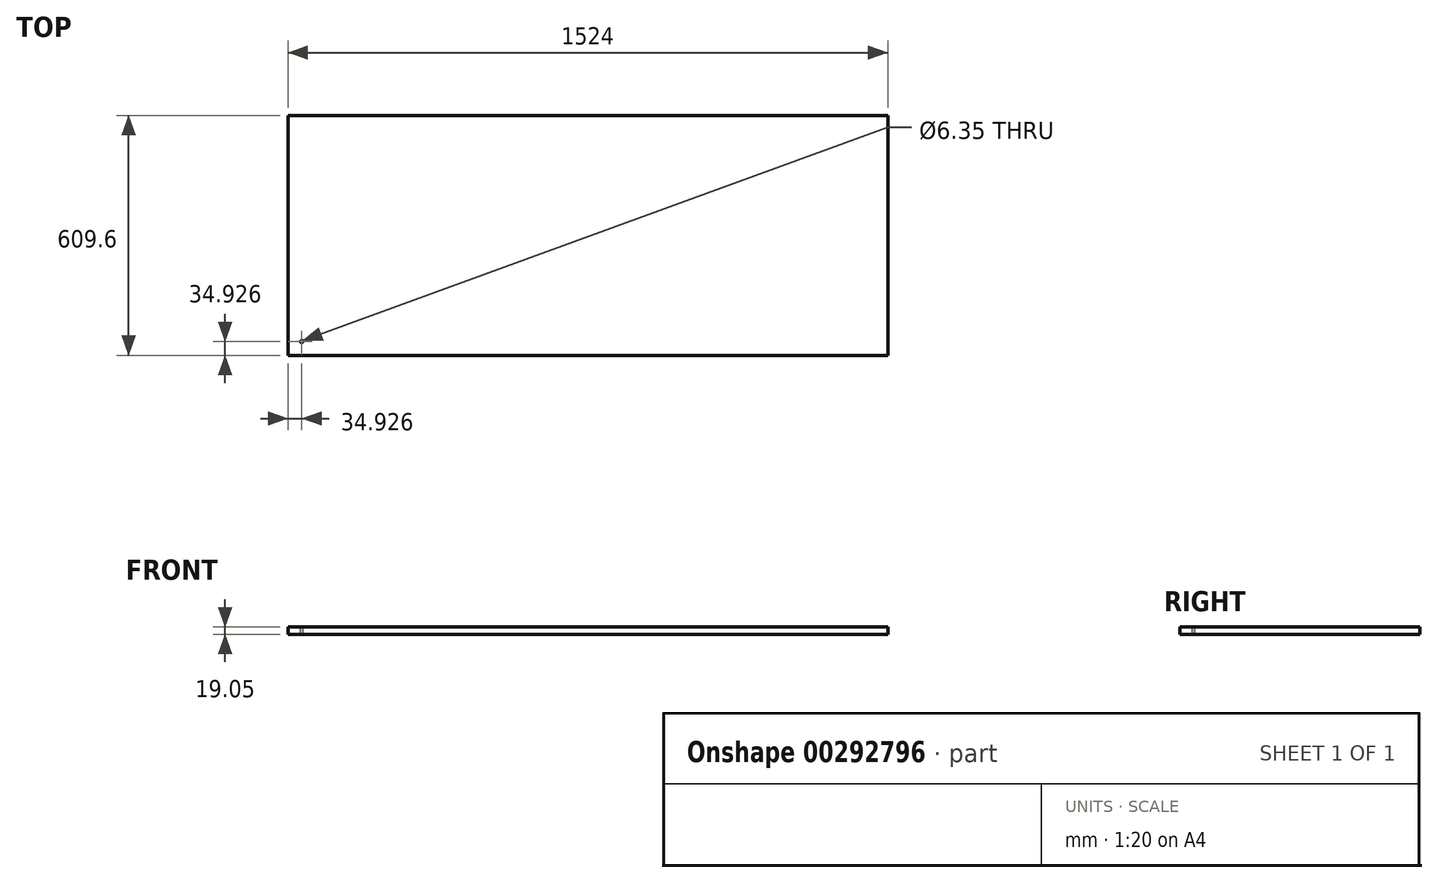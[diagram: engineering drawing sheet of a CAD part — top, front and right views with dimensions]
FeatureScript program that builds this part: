
annotation { "Feature Type Name" : "Feature", "Feature Type Description" : "" }
export const myFeature = defineFeature(function(context is Context, id is Id, definition is map)
    precondition{}
    {
        {
            var Q0;
            Q0=qCreatedBy(makeId("Top.planeOp"),FACE);
            var sketch = newSketch(context, id + "F0", { "sketchPlane" : qUnion([Q0])});
            skLineSegment(sketch, "E0.bottom", {"start": v(-1132.59, -308.04) * mm, "end": v(391.41, -308.04) * mm});
            skLineSegment(sketch, "E0.top", {"start": v(-1132.59, 301.56) * mm, "end": v(391.41, 301.56) * mm});
            skLineSegment(sketch, "E0.left", {"start": v(-1132.59, -308.04) * mm, "end": v(-1132.59, 301.56) * mm});
            skLineSegment(sketch, "E0.right", {"start": v(391.41, -308.04) * mm, "end": v(391.41, 301.56) * mm});
            skSolve(sketch);
        }
        {
            var Q0;
            Q0 = qSketchRegion(id + "F0", true);
            extrude(context, id + "F1", {"entities" : qUnion([Q0]), "depth" : 19.05 * mm});
        }
        {
            var Q0;
            Q0=makeQuery(id+"F1.opExtrude","CAP_FACE",FACE,{"disambiguationData":[OSD([sQuery(id+"F0.wireOp",EDGE,"E0.bottom"),sQuery(id+"F0.wireOp",EDGE,"E0.top"),sQuery(id+"F0.wireOp",EDGE,"E0.left"),sQuery(id+"F0.wireOp",EDGE,"E0.right")])],"isStart":false});
            var sketch = newSketch(context, id + "F2", { "sketchPlane" : qUnion([Q0])});
            skCircle(sketch, "E1", {"center": v(-1097.66, -273.11) * mm, "radius": 3.18 * mm});
            skSolve(sketch);
        }
        {
            var Q0;
            Q0=sQuery(id+"F2.wireOp",VERTEX,"E1.center");
            var Q1;
            Q1=makeQuery(id+"F1.opExtrude","SWEPT_BODY",BODY,{"disambiguationData":[OSD([sQuery(id+"F0.wireOp",EDGE,"E0.bottom"),sQuery(id+"F0.wireOp",EDGE,"E0.top"),sQuery(id+"F0.wireOp",EDGE,"E0.left"),sQuery(id+"F0.wireOp",EDGE,"E0.right")])]});
            hole(context, id + "F3", {"style" : HoleStyle.SIMPLE, "endStyle" : HoleEndStyle.THROUGH, "holeDiameter" : 6.35 * mm, "tappedDepth" : 12.7 * mm, "tapClearance" : 3, "locations" : qUnion([Q0]), "scope" : qUnion([Q1])});
        }
    });
